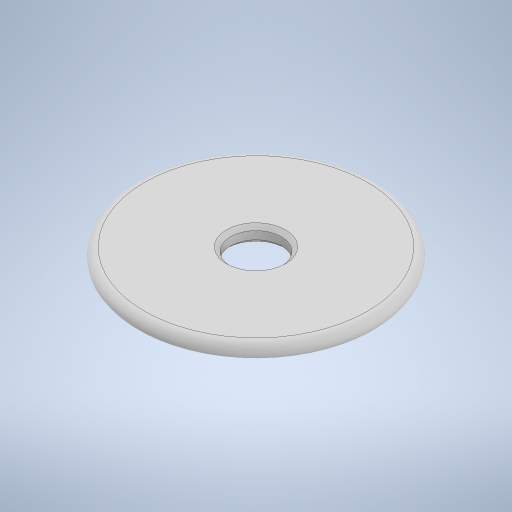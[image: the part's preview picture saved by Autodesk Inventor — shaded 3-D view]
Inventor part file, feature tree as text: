
AUTODESK INVENTOR PART (.ipt)
format: ipt  version: 2024.2 (Build 282272000, 272)  size: 247,296 bytes
history: native  units: mm
features: extrude x2, plane x1, fillet x1, chamfer x1
ambient origin geometry x8: Origin, YZ Plane, XZ Plane, XY Plane, X Axis, Y Axis, Z Axis, Center Point
bodies: Solid1 (feature_tree)
feature tree (5):
  extrude  "Extrusion1"  Depth=15.0mm
  plane  "Work Plane1"
  extrude  "Extrusion3"  Depth=1.0mm TaperAngle=0.0deg
  fillet  "Fillet2"  Radius=3.2mm
  chamfer  "Chamfer2"  Distance=10.0mm
